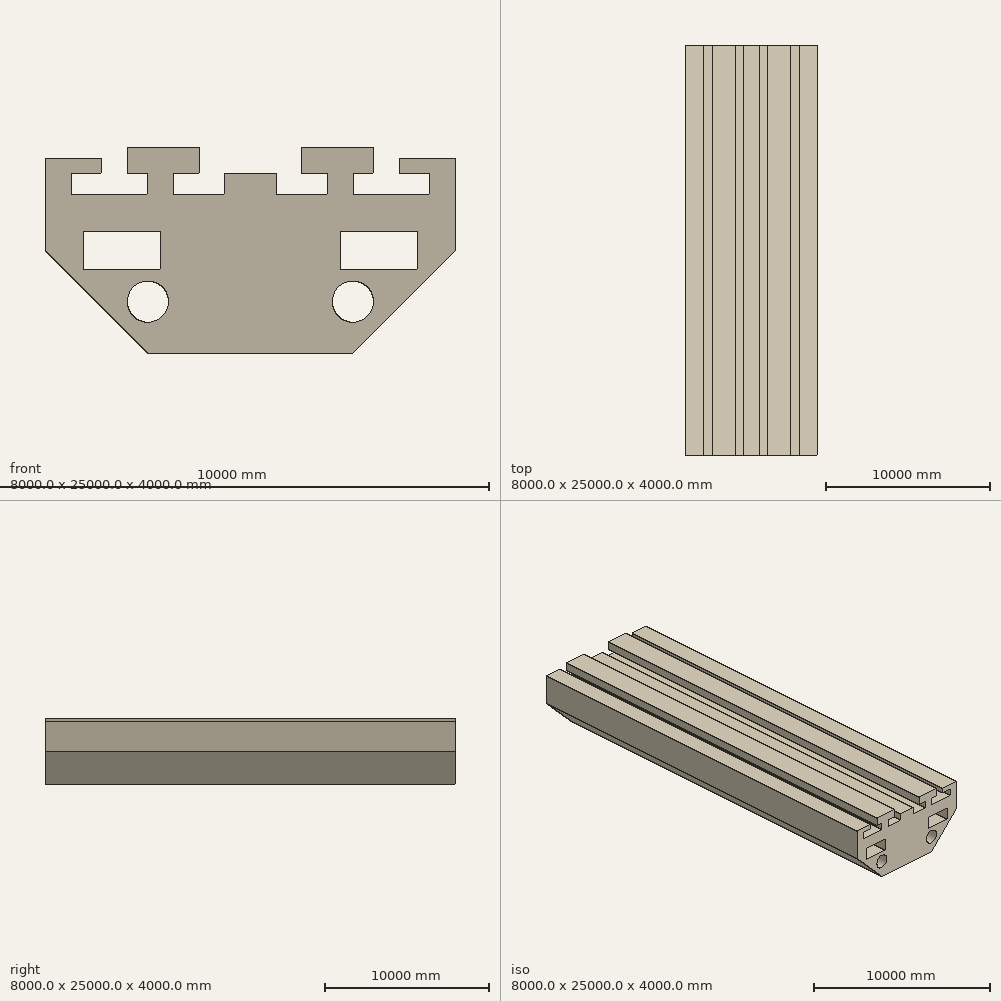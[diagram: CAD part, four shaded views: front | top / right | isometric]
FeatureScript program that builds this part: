
annotation { "Feature Type Name" : "Feature", "Feature Type Description" : "" }
export const myFeature = defineFeature(function(context is Context, id is Id, definition is map)
    precondition{}
    {
        {
            var Q0;
            Q0=qCreatedBy(makeId("Front.planeOp"),FACE);
            var sketch = newSketch(context, id + "F0", { "sketchPlane" : qUnion([Q0])});
            skLineSegment(sketch, "E0.top", {"start": v(0, -2000) * mm, "end": v(-2000, -2000) * mm});
            skLineSegment(sketch, "E0.right", {"start": v(-4000, 1800) * mm, "end": v(-4000, 0) * mm});
            skPoint(sketch, "E0.middle", {"position": v(0, 0) * mm});
            skLineSegment(sketch, "E1", {"start": v(-4000, 0) * mm, "end": v(-2000, -2000) * mm});
            skPoint(sketch, "E2.MirrorP", {"position": v(-4000, -4000) * mm});
            skLineSegment(sketch, "E3.bottom", {"start": v(-1750, 375) * mm, "end": v(-3250, 375) * mm});
            skLineSegment(sketch, "E3.top", {"start": v(-1750, -375) * mm, "end": v(-3250, -375) * mm});
            skLineSegment(sketch, "E3.left", {"start": v(-1750, 375) * mm, "end": v(-1750, -375) * mm});
            skLineSegment(sketch, "E3.right", {"start": v(-3250, 375) * mm, "end": v(-3250, -375) * mm});
            skPoint(sketch, "E3.middle", {"position": v(-2500, 0) * mm});
            skCircle(sketch, "E4", {"center": v(-2000, -1000) * mm, "radius": 400 * mm});
            skLineSegment(sketch, "E5.right", {"start": v(-2400, 2000) * mm, "end": v(-2400, 1500) * mm});
            skLineSegment(sketch, "E6.trimOffspring", {"start": v(-2900, 1800) * mm, "end": v(-4000, 1800) * mm});
            skLineSegment(sketch, "E7", {"start": v(-2400, 1500) * mm, "end": v(-2000, 1500) * mm});
            skLineSegment(sketch, "E8", {"start": v(-2000, 1100) * mm, "end": v(-3500, 1100) * mm});
            skLineSegment(sketch, "E9", {"start": v(-3500, 1100) * mm, "end": v(-3500, 1500) * mm});
            skLineSegment(sketch, "E10", {"start": v(-3500, 1500) * mm, "end": v(-2900, 1500) * mm});
            skLineSegment(sketch, "E11", {"start": v(-2900, 1500) * mm, "end": v(-2900, 1800) * mm});
            skLineSegment(sketch, "E12.trimOffspring", {"start": v(-1000, 2000) * mm, "end": v(-2400, 2000) * mm});
            skLineSegment(sketch, "E13", {"start": v(0, -2000) * mm, "end": v(0, 1500) * mm});
            skLineSegment(sketch, "E14", {"start": v(-500, 1500) * mm, "end": v(-500, 1100) * mm});
            skLineSegment(sketch, "E15", {"start": v(-500, 1100) * mm, "end": v(-1500, 1100) * mm});
            skLineSegment(sketch, "E16", {"start": v(-1500, 1100) * mm, "end": v(-1500, 1500) * mm});
            skLineSegment(sketch, "E17", {"start": v(-1500, 1500) * mm, "end": v(-1000, 1500) * mm});
            skLineSegment(sketch, "E18", {"start": v(-1000, 1500) * mm, "end": v(-1000, 2000) * mm});
            skLineSegment(sketch, "E19", {"start": v(-500, 1500) * mm, "end": v(0, 1500) * mm});
            skLineSegment(sketch, "E20", {"start": v(-2000, 1100) * mm, "end": v(-2000, 1500) * mm});
            skSolve(sketch);
        }
        {
            var Q0;
            Q0 = qSketchRegion(id + "F0", true);
            extrude(context, id + "F1", {"entities" : qUnion([Q0]), "endBound" : BoundingType.SYMMETRIC, "depth" : 25000 * mm, "offsetDistance" : 25 * mm});
        }
        {
            var Q0;
            Q0=makeQuery(id+"F1.opExtrude","SWEPT_BODY",BODY,{"disambiguationData":[OSD([sQuery(id+"F0.wireOp",EDGE,"E0.top"),sQuery(id+"F0.wireOp",EDGE,"E0.right"),sQuery(id+"F0.wireOp",EDGE,"E1"),sQuery(id+"F0.wireOp",EDGE,"E3.bottom"),sQuery(id+"F0.wireOp",EDGE,"E3.top"),sQuery(id+"F0.wireOp",EDGE,"E3.left"),sQuery(id+"F0.wireOp",EDGE,"E3.right"),sQuery(id+"F0.wireOp",EDGE,"E4"),sQuery(id+"F0.wireOp",EDGE,"E5.right"),sQuery(id+"F0.wireOp",EDGE,"E6.trimOffspring"),sQuery(id+"F0.wireOp",EDGE,"E7"),sQuery(id+"F0.wireOp",EDGE,"E8"),sQuery(id+"F0.wireOp",EDGE,"E9"),sQuery(id+"F0.wireOp",EDGE,"E10"),sQuery(id+"F0.wireOp",EDGE,"E11"),sQuery(id+"F0.wireOp",EDGE,"E12.trimOffspring"),sQuery(id+"F0.wireOp",EDGE,"E13"),sQuery(id+"F0.wireOp",EDGE,"E14"),sQuery(id+"F0.wireOp",EDGE,"E15"),sQuery(id+"F0.wireOp",EDGE,"E16"),sQuery(id+"F0.wireOp",EDGE,"E17"),sQuery(id+"F0.wireOp",EDGE,"E18"),sQuery(id+"F0.wireOp",EDGE,"E19"),sQuery(id+"F0.wireOp",EDGE,"E20")])]});
            var Q1;
            Q1=makeQuery(id+"F1.opExtrude","SWEPT_FACE",FACE,{"disambiguationData":[OSD([sQuery(id+"F0.wireOp",EDGE,"E13")])]});
            mirror(context, id + "F2", {"operationType" : NewBodyOperationType.ADD, "entities" : qUnion([Q0]), "mirrorPlane" : qUnion([Q1])});
        }
    });
